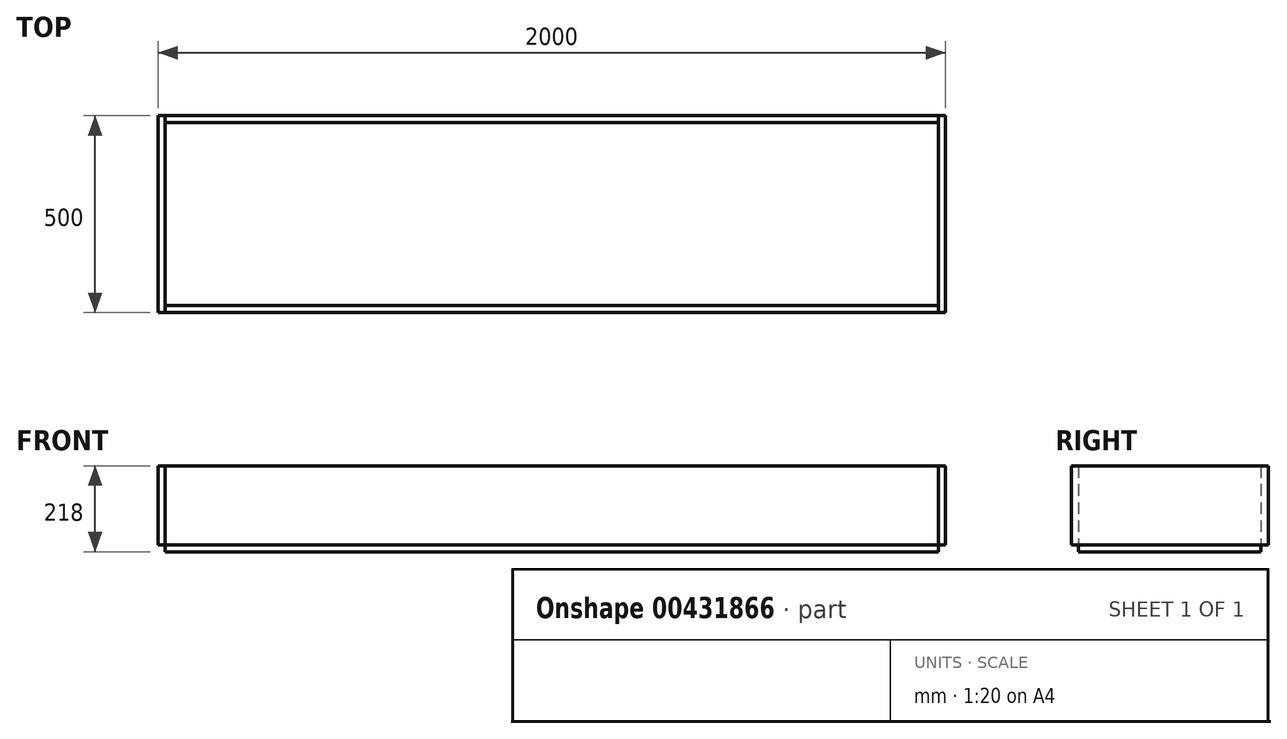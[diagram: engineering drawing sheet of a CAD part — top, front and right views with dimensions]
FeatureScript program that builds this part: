
annotation { "Feature Type Name" : "Feature", "Feature Type Description" : "" }
export const myFeature = defineFeature(function(context is Context, id is Id, definition is map)
    precondition{}
    {
        {
            var Q0;
            Q0=qCreatedBy(makeId("Top.planeOp"),FACE);
            var sketch = newSketch(context, id + "F0", { "sketchPlane" : qUnion([Q0])});
            skLineSegment(sketch, "E0.bottom", {"start": v(-1941.94, 431.08) * mm, "end": v(58.06, 431.08) * mm});
            skLineSegment(sketch, "E0.top", {"start": v(-1941.94, -68.92) * mm, "end": v(58.06, -68.92) * mm});
            skLineSegment(sketch, "E0.left", {"start": v(-1941.94, 431.08) * mm, "end": v(-1941.94, -68.92) * mm});
            skLineSegment(sketch, "E0.right", {"start": v(58.06, 431.08) * mm, "end": v(58.06, -68.92) * mm});
            skLineSegment(sketch, "E1.bottom", {"start": v(-1923.94, 413.08) * mm, "end": v(40.06, 413.08) * mm});
            skLineSegment(sketch, "E1.top", {"start": v(-1923.94, -50.92) * mm, "end": v(40.06, -50.92) * mm});
            skLineSegment(sketch, "E1.left", {"start": v(-1923.94, 413.08) * mm, "end": v(-1923.94, -50.92) * mm});
            skLineSegment(sketch, "E1.right", {"start": v(40.06, 413.08) * mm, "end": v(40.06, -50.92) * mm});
            skLineSegment(sketch, "E2", {"start": v(-1923.94, 413.08) * mm, "end": v(-1923.94, 431.08) * mm});
            skLineSegment(sketch, "E3", {"start": v(-1923.94, -50.92) * mm, "end": v(-1923.94, -68.92) * mm});
            skLineSegment(sketch, "E4", {"start": v(40.06, -50.92) * mm, "end": v(40.06, -68.92) * mm});
            skLineSegment(sketch, "E5", {"start": v(40.06, 413.08) * mm, "end": v(40.06, 431.08) * mm});
            skSolve(sketch);
        }
        {
            var Q0;
            {var subQ0=sQuery(id+"F0.wireOp",EDGE,"E0.left");Q0=makeQuery(id+"F0.imprint","IMPRINT",FACE,{"disambiguationData":[TD([[makeQuery(id+"F0.imprint","IMPRINT",EDGE,{"derivedFrom":subQ0}),1.0]])]});}
            var Q1;
            {var subQ0=sQuery(id+"F0.wireOp",EDGE,"E0.right");Q1=makeQuery(id+"F0.imprint","IMPRINT",FACE,{"disambiguationData":[TD([[makeQuery(id+"F0.imprint","IMPRINT",EDGE,{"derivedFrom":subQ0}),-1.0]])]});}
            extrude(context, id + "F1", {"entities" : qUnion([Q0, Q1]), "depth" : 200 * mm, "offsetDistance" : 25 * mm});
        }
        {
            var Q0;
            Q0=makeQuery(id+"F0.imprint","IMPRINT",FACE,{"disambiguationData":[TD([[makeQuery(id+"F0.imprint","IMPRINT",EDGE,{"derivedFrom":sQuery(id+"F0.wireOp",EDGE,"E1.bottom")}),1.0]])]});
            var Q1;
            Q1=makeQuery(id+"F0.imprint","IMPRINT",FACE,{"disambiguationData":[TD([[makeQuery(id+"F0.imprint","IMPRINT",EDGE,{"derivedFrom":sQuery(id+"F0.wireOp",EDGE,"E1.top")}),-1.0]])]});
            extrude(context, id + "F2", {"entities" : qUnion([Q0, Q1]), "depth" : 200 * mm, "offsetDistance" : 25 * mm});
        }
        {
            var Q0;
            Q0=makeQuery(id+"F0.imprint","IMPRINT",FACE,{"disambiguationData":[TD([[makeQuery(id+"F0.imprint","IMPRINT",EDGE,{"derivedFrom":sQuery(id+"F0.wireOp",EDGE,"E1.bottom")}),-1.0]])]});
            extrude(context, id + "F3", {"entities" : qUnion([Q0]), "oppositeDirection" : true, "depth" : 18 * mm, "offsetDistance" : 25 * mm});
        }
        {
            var Q0;
            Q0=sQuery(id+"F0.wireOp",EDGE,"E0.left");
            var Q1;
            Q1=sQuery(id+"F0.wireOp",EDGE,"E0.top");
            var Q2;
            Q2=sQuery(id+"F0.wireOp",EDGE,"E0.bottom");
            var Q3;
            Q3=sQuery(id+"F0.wireOp",EDGE,"E0.right");
            extrude(context, id + "F4", {"bodyType" : ToolBodyType.SURFACE, "surfaceEntities" : qUnion([Q0, Q1, Q2, Q3]), "oppositeDirection" : true, "depth" : 18 * mm, "offsetDistance" : 25 * mm});
        }
    });
